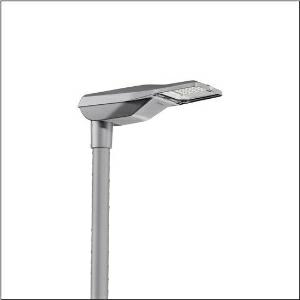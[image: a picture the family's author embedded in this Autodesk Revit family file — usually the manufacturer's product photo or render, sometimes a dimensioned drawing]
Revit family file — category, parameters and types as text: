
# Revit family: streetlight_sl_21_iq_micro___st0_8a_5xe1c41g08db_305a
name_source: partatom
category: Lighting Fixtures
units: mm (PartAtom-declared; Revit-internal decimal feet)

## family parameters
Cut with Voids When Loaded = No
Host = Face
Light Source = No
Part Type = Normal
Room Calculation Point = No
Round Connector Dimension = Use Diameter
Shared = No

## types (1)
- --- (1 x LED, 5010 lm, 36.4 W, 4000K)
    Apparent Load = 36 VA
    CIE Flux Codes = 38 75 97 100 100
    Color Rendering = 70
    Color Temperature = 4000K
    Default Elevation = 1800 mm
    Description = Streetlight SL 21 iQ micro, mast luminaire, primary light control with lens, of PMMA, primary optical cover: cover, of toughened safety glass, transparent, light distribution: ST0.8a, light emission: direct distribution, primary light characteristic: asymmetric, installation type: post-top, side-entry, LED, High Power LED, rated luminous flux: 5.010lm, luminous efficacy: 138lm/W, light colour: 740, colour temperature: 4000K, control gear: iQ Street-Remote, control: Street-Remote, Auto-Match, Temp-Guard, Lumen-Switch, Night-Set, Smart-Wire, Light-Fading, Desk-Remote (wireless, voltage-free reading and setting of iQ features in the workshop via application-optimized NFC function/RFID function), optimised constant luminous flux control (CLO 2.0), pre-setting: linear dimming characteristic, mains connection: 220..240V, AC, 50/60Hz, start of lifetime: 36W, end of service life: 38W, reduction: 16W, luminaire housing, of diecast aluminium, powder-coated, SITECO metallic grey (DB 702S), corrosivity category C5 high according to DIN EN ISO 12944, please order mast flange separately, inclination adjustable: 0°, 5°, 10°, 15°, sealing non-destructively replaceable, multi-level sealing system, length: 528mm, width: 235mm, height: 110mm, mast flange for spigot size: 42mm (side-entry): 5XC10008XM4, 60/48mm (side-entry/post-top): 5XC10108XM2, 76/60mm (side-entry/post-top): 5XC10108XM1, protection rating (complete): IP66, insulation class (complete): insulation class II (safety insulation), certification: CE, ENEC, ENEC+, VDE, impact resistance: IK10, permissible operating ambient temperature for outdoor applications: -40..+50°C, standard-compliant lighting for roads and squares, packaging unit: 1 piece

Light Distribution: ST0.8a
    Height = 110 mm
    Lamp = 1 x LED
    Lamp Light Flux = 5010 lm
    Lamp Power = 36.4 W
    Lamp count = 1
    Length = 528 mm
    Luminous efficacy = 138 lm/W
    Manufacturer = Siteco
    ModVariant = No
    Model = 5XE1C41G08DB
    Number of Poles = 1
    OnlyDefault = Yes
    Power Factor = 1
    Product Name = Streetlight SL 21 iQ micro | ST0.8a
    Product group = mast luminaire | pylon top
    ProductGroupID = 6100
    Protection Class = Protection class II
    Protection Degree = IP 66
    RLX_Detail_Level = 1
    RLX_Emergency_Light_Flux = 0 lm
    RLX_Emergency_Type = 0
    RLX_Emergency_Type_DB = No
    RlxData = <blob elided: 99121 chars, md5=4d118689>
    Socket = socket
    Standby Power = 0 W
    System Light Flux = 5010 lm
    System Power = 36 W
    Type Comments = factory setting: luminous flux: 100 % | dim-lin: 254 | 715 mA
    Type Image = l_1006881.jpg
    URL = http://relux.com
    VarID = @adj_153957
    Voltage = 0 V
    Weight = 0.00 kg
    Width = 235 mm

## geometry (parser evidence)
native form markers: Blend x4, Sweep x10
no freeform markers — native parametric forms only
